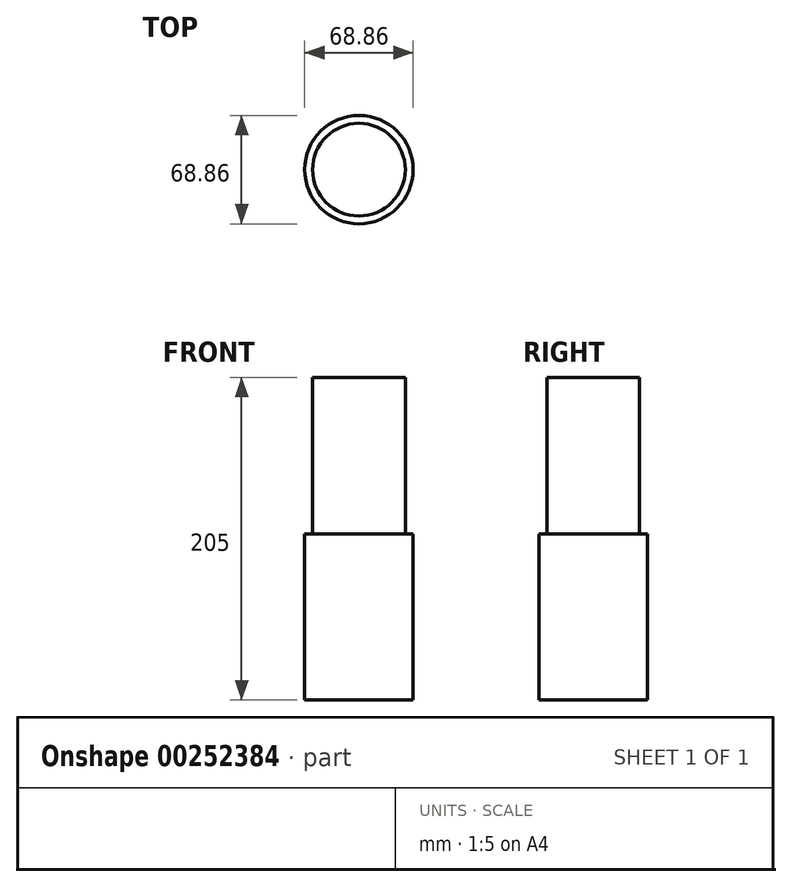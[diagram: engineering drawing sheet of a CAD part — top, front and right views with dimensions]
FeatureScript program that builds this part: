
annotation { "Feature Type Name" : "Feature", "Feature Type Description" : "" }
export const myFeature = defineFeature(function(context is Context, id is Id, definition is map)
    precondition{}
    {
        {
            var Q0;
            Q0=qCreatedBy(makeId("Front.planeOp"),FACE);
            var sketch = newSketch(context, id + "F0", { "sketchPlane" : qUnion([Q0])});
            skLineSegment(sketch, "E0.bottom", {"start": v(-34.43, 40.3) * mm, "end": v(32.42, 40.3) * mm});
            skLineSegment(sketch, "E0.top", {"start": v(-34.43, -65.27) * mm, "end": v(32.42, -65.27) * mm});
            skLineSegment(sketch, "E0.left", {"start": v(-34.43, 40.3) * mm, "end": v(-34.43, -65.27) * mm});
            skLineSegment(sketch, "E0.right", {"start": v(32.42, 40.3) * mm, "end": v(32.42, -65.27) * mm});
            skLineSegment(sketch, "E1", {"start": v(0, 40.3) * mm, "end": v(0, -65.27) * mm});
            skSolve(sketch);
        }
        {
            var Q0;
            {var subQ0=sQuery(id+"F0.wireOp",EDGE,"E0.left");Q0=makeQuery(id+"F0.imprint","IMPRINT",FACE,{"disambiguationData":[TD([[makeQuery(id+"F0.imprint","IMPRINT",EDGE,{"derivedFrom":subQ0}),1.0]])]});}
            var Q1;
            Q1=sQuery(id+"F0.wireOp",EDGE,"E1");
            revolve(context, id + "F1", {"entities" : qUnion([Q0]), "axis" : qUnion([Q1]), "revolveType" : RevolveType.FULL});
        }
        {
            var Q0;
            Q0=makeQuery(id+"F1.opRevolve","SWEPT_FACE",FACE,{"disambiguationData":[OSD([sQuery(id+"F0.wireOp",EDGE,"E0.bottom")])]});
            var Q1;
            Q1=makeQuery(id+"F1.opRevolve","SWEPT_BODY",BODY,{"disambiguationData":[OSD([sQuery(id+"F0.wireOp",EDGE,"E0.bottom"),sQuery(id+"F0.wireOp",EDGE,"E0.top"),sQuery(id+"F0.wireOp",EDGE,"E0.left"),sQuery(id+"F0.wireOp",EDGE,"E1")])]});
            shell(context, id + "F2", {"entities" : qUnion([Q0]), "parts" : qUnion([Q1]), "thickness" : 5 * mm});
        }
        {
            var Q0;
            Q0=makeQuery(id+"F2.opShell","OFFSET_FACE",FACE,{"disambiguationData":[OSD([sQuery(id+"F0.wireOp",EDGE,"E0.top")])]});
            extrude(context, id + "F3", {"entities" : qUnion([Q0]), "operationType" : NewBodyOperationType.ADD, "depth" : 200 * mm});
        }
    });
